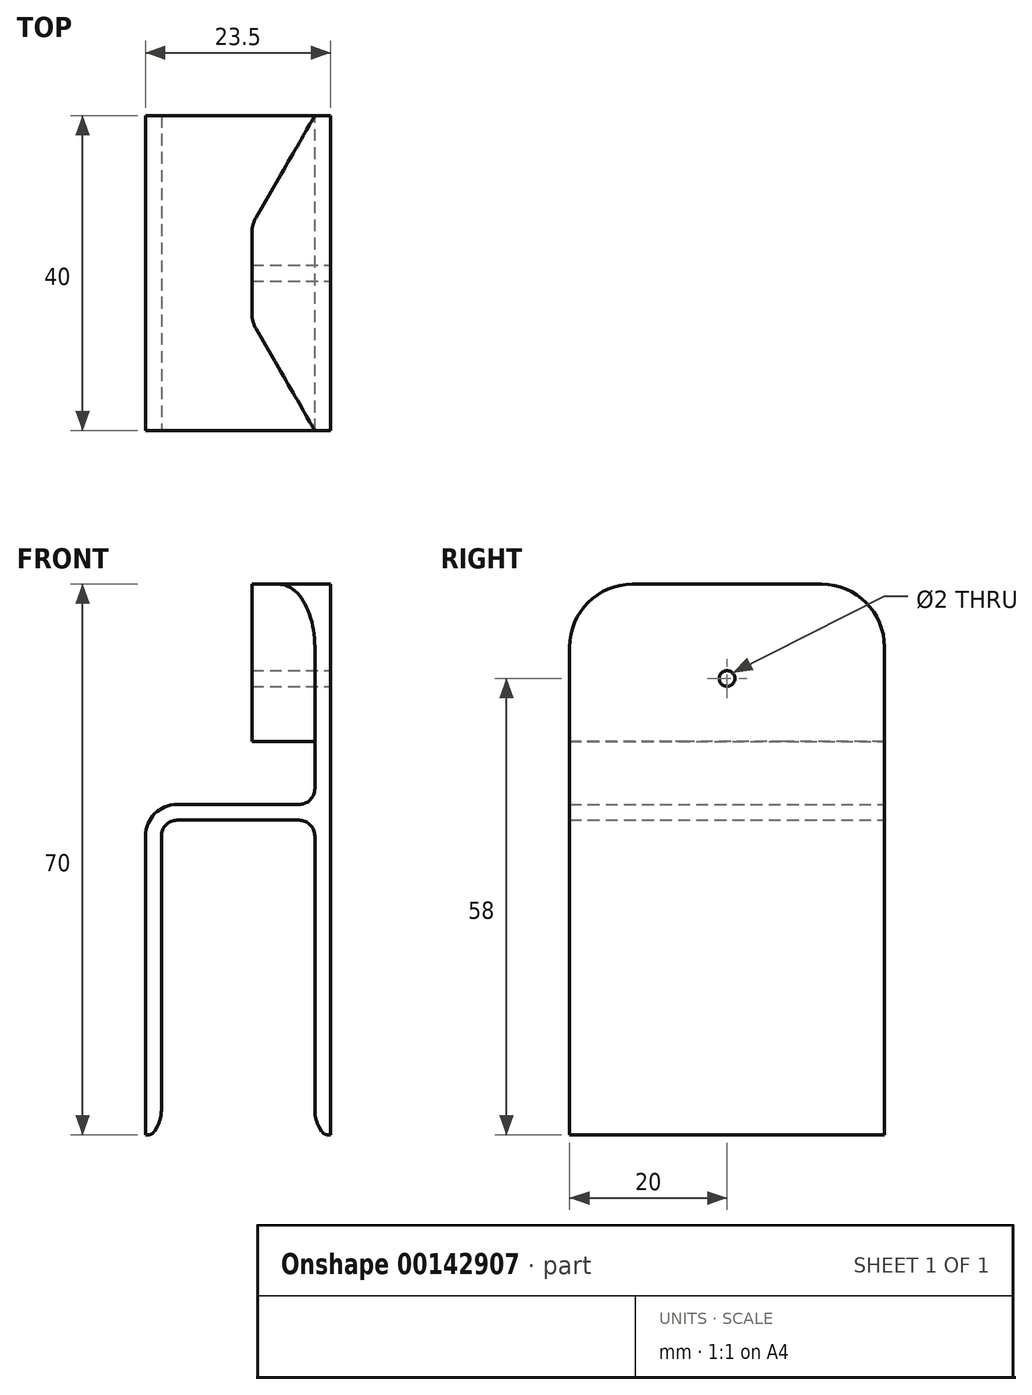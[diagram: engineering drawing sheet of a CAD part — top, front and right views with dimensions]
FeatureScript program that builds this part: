
annotation { "Feature Type Name" : "Feature", "Feature Type Description" : "" }
export const myFeature = defineFeature(function(context is Context, id is Id, definition is map)
    precondition{}
    {
        {
            var Q0;
            Q0=qCreatedBy(makeId("Front.planeOp"),FACE);
            var sketch = newSketch(context, id + "F0", { "sketchPlane" : qUnion([Q0])});
            skLineSegment(sketch, "E0", {"start": v(-19.5, 0) * mm, "end": v(-19.5, -40) * mm});
            skLineSegment(sketch, "E1", {"start": v(-19.5, 0) * mm, "end": v(0, 0) * mm});
            skLineSegment(sketch, "E2", {"start": v(0, 30) * mm, "end": v(0, -40) * mm});
            skLineSegment(sketch, "E3.0", {"start": v(2, 30) * mm, "end": v(2, -40) * mm});
            skLineSegment(sketch, "E4.0", {"start": v(-21.5, 2) * mm, "end": v(0, 2) * mm});
            skLineSegment(sketch, "E5.0", {"start": v(-21.5, 2) * mm, "end": v(-21.5, -40) * mm});
            skLineSegment(sketch, "E6", {"start": v(0, -40) * mm, "end": v(2, -40) * mm});
            skLineSegment(sketch, "E7", {"start": v(-19.5, -40) * mm, "end": v(-21.5, -40) * mm});
            skLineSegment(sketch, "E8", {"start": v(0, 30) * mm, "end": v(2, 30) * mm});
            skSolve(sketch);
        }
        {
            var Q0;
            Q0=makeQuery(id+"F0.imprint","IMPRINT",FACE,{"disambiguationData":[TD([[makeQuery(id+"F0.imprint","IMPRINT",EDGE,{"derivedFrom":sQuery(id+"F0.wireOp",EDGE,"E3.0")}),-1.0]])]});
            var Q1;
            Q1=makeQuery(id+"F0.imprint","IMPRINT",FACE,{"disambiguationData":[TD([[makeQuery(id+"F0.imprint","IMPRINT",EDGE,{"derivedFrom":sQuery(id+"F0.wireOp",EDGE,"E0")}),-1.0]])]});
            extrude(context, id + "F1", {"entities" : qUnion([Q0, Q1]), "depth" : 40 * mm, "symmetric" : true});
        }
        {
            var Q0;
            Q0=makeQuery(id+"F1.opExtrude","SWEPT_FACE",FACE,{"disambiguationData":[OSD([sQuery(id+"F0.wireOp",EDGE,"E8")])]});
            var sketch = newSketch(context, id + "F2", { "sketchPlane" : qUnion([Q0])});
            skLineSegment(sketch, "E9", {"start": v(0, 20) * mm, "end": v(-8, 6.14) * mm});
            skLineSegment(sketch, "E10", {"start": v(-8, 6.14) * mm, "end": v(-8, -6.14) * mm});
            skLineSegment(sketch, "E11", {"start": v(-8, -6.14) * mm, "end": v(0, -20) * mm});
            skSolve(sketch);
        }
        {
            var Q0;
            Q0=makeQuery(id+"F2.imprint","IMPRINT",FACE,{"disambiguationData":[TD([[makeQuery(id+"F2.imprint","IMPRINT",EDGE,{"derivedFrom":sQuery(id+"F2.wireOp",EDGE,"E9")}),1.0]])]});
            extrude(context, id + "F3", {"entities" : qUnion([Q0]), "operationType" : NewBodyOperationType.ADD, "oppositeDirection" : true, "depth" : 20 * mm});
        }
        {
            var Q0;
            Q0=makeQuery(id+"F1.opExtrude","SWEPT_FACE",FACE,{"disambiguationData":[OSD([sQuery(id+"F0.wireOp",EDGE,"E3.0")])]});
            var sketch = newSketch(context, id + "F4", { "sketchPlane" : qUnion([Q0])});
            skLineSegment(sketch, "E12.0", {"start": v(-20, 30) * mm, "end": v(20, 30) * mm});
            skLineSegment(sketch, "E13", {"start": v(0, 30) * mm, "end": v(0, 18) * mm});
            skPoint(sketch, "E13.endSnap0", {"position": v(0, 30) * mm});
            skPoint(sketch, "E14", {"position": v(0, 18) * mm});
            skSolve(sketch);
        }
        {
            var Q0;
            Q0=sQuery(id+"F4.wireOp",VERTEX,"E14");
            var Q1;
            Q1=makeQuery(id+"F1.opExtrude","SWEPT_BODY",BODY,{"disambiguationData":[OSD([sQuery(id+"F0.wireOp",EDGE,"E0"),sQuery(id+"F0.wireOp",EDGE,"E1"),sQuery(id+"F0.wireOp",EDGE,"E2"),sQuery(id+"F0.wireOp",EDGE,"E3.0"),sQuery(id+"F0.wireOp",EDGE,"E4.0"),sQuery(id+"F0.wireOp",EDGE,"E5.0"),sQuery(id+"F0.wireOp",EDGE,"E6"),sQuery(id+"F0.wireOp",EDGE,"E7"),sQuery(id+"F0.wireOp",EDGE,"E8")])]});
            hole(context, id + "F5", {"style" : HoleStyle.SIMPLE, "endStyle" : HoleEndStyle.THROUGH, "holeDiameter" : 2 * mm, "startFromSketch" : true, "locations" : qUnion([Q0]), "scope" : qUnion([Q1]), "isTappedThrough" : true});
        }
        {
            var Q0;
            Q0=makeQuery(id+"F1.opExtrude","SWEPT_EDGE",EDGE,{"disambiguationData":[OSD([sQuery(id+"F0.wireOp",EDGE,"E0"),sQuery(id+"F0.wireOp",EDGE,"E7")])]});
            chamfer(context, id + "F6", {"entities" : qUnion([Q0]), "chamferType" : ChamferType.OFFSET_ANGLE, "width" : 2 * mm, "oppositeDirection" : false, "angle" : 30 * degree});
        }
        {
            var Q0;
            Q0=makeQuery(id+"F1.opExtrude","SWEPT_EDGE",EDGE,{"disambiguationData":[OSD([sQuery(id+"F0.wireOp",EDGE,"E2"),sQuery(id+"F0.wireOp",EDGE,"E6")])]});
            chamfer(context, id + "F7", {"entities" : qUnion([Q0]), "chamferType" : ChamferType.OFFSET_ANGLE, "width" : 2 * mm, "oppositeDirection" : true, "angle" : 30 * degree});
        }
        {
            var Q0;
            {var subQ0=sQuery(id+"F0.wireOp",EDGE,"E7");Q0=makeQuery(id+"F6.opChamfer","BLEND_EDGE",EDGE,{"blendedFrom":[makeQuery(id+"F1.opExtrude","SWEPT_EDGE",EDGE,{"disambiguationData":[OSD([sQuery(id+"F0.wireOp",EDGE,"E0"),subQ0])]}),makeQuery(id+"F1.opExtrude","SWEPT_FACE",FACE,{"disambiguationData":[OSD([subQ0])]})],"blendedInto":[makeQuery(id+"F1.opExtrude","SWEPT_FACE",FACE,{"disambiguationData":[OSD([subQ0])]})]});}
            var Q1;
            {var subQ0=sQuery(id+"F0.wireOp",EDGE,"E6");Q1=makeQuery(id+"F7.opChamfer","BLEND_EDGE",EDGE,{"blendedFrom":[makeQuery(id+"F1.opExtrude","SWEPT_EDGE",EDGE,{"disambiguationData":[OSD([sQuery(id+"F0.wireOp",EDGE,"E2"),subQ0])]}),makeQuery(id+"F1.opExtrude","SWEPT_FACE",FACE,{"disambiguationData":[OSD([subQ0])]})],"blendedInto":[makeQuery(id+"F1.opExtrude","SWEPT_FACE",FACE,{"disambiguationData":[OSD([subQ0])]})]});}
            fillet(context, id + "F8", {"entities" : qUnion([Q0, Q1]), "radius" : 1 * mm, "tangentPropagation" : true, "allowEdgeOverflow" : false});
        }
        {
            var Q0;
            Q0=makeQuery(id+"F1.opExtrude","SWEPT_EDGE",EDGE,{"disambiguationData":[OSD([sQuery(id+"F0.wireOp",EDGE,"E2"),sQuery(id+"F0.wireOp",EDGE,"E4.0")])]});
            var Q1;
            Q1=makeQuery(id+"F1.opExtrude","SWEPT_EDGE",EDGE,{"disambiguationData":[OSD([sQuery(id+"F0.wireOp",EDGE,"E0"),sQuery(id+"F0.wireOp",EDGE,"E1")])]});
            var Q2;
            Q2=makeQuery(id+"F1.opExtrude","SWEPT_EDGE",EDGE,{"disambiguationData":[OSD([sQuery(id+"F0.wireOp",EDGE,"E1"),sQuery(id+"F0.wireOp",EDGE,"E2")])]});
            var Q3;
            Q3=makeQuery(id+"F3.opExtrude","CAP_EDGE",EDGE,{"disambiguationData":[OSD([sQuery(id+"F0.wireOp",EDGE,"E2"),sQuery(id+"F0.wireOp",EDGE,"E8")])],"isStart":false});
            fillet(context, id + "F9", {"entities" : qUnion([Q0, Q1, Q2, Q3]), "radius" : 2 * mm, "tangentPropagation" : true, "allowEdgeOverflow" : false});
        }
        {
            var Q0;
            Q0=makeQuery(id+"F1.opExtrude","SWEPT_EDGE",EDGE,{"disambiguationData":[OSD([sQuery(id+"F0.wireOp",EDGE,"E4.0"),sQuery(id+"F0.wireOp",EDGE,"E5.0")])]});
            var Q1;
            Q1=makeQuery(id+"F3.opExtrude","SWEPT_EDGE",EDGE,{"disambiguationData":[OSD([sQuery(id+"F2.wireOp",EDGE,"E10"),sQuery(id+"F2.wireOp",EDGE,"E11")])]});
            var Q2;
            Q2=makeQuery(id+"F3.opExtrude","SWEPT_EDGE",EDGE,{"disambiguationData":[OSD([sQuery(id+"F2.wireOp",EDGE,"E9"),sQuery(id+"F2.wireOp",EDGE,"E10")])]});
            var Q3;
            {var subQ0=sQuery(id+"F0.wireOp",EDGE,"E0");Q3=makeQuery(id+"F6.opChamfer","BLEND_EDGE",EDGE,{"blendedFrom":[makeQuery(id+"F1.opExtrude","SWEPT_EDGE",EDGE,{"disambiguationData":[OSD([subQ0,sQuery(id+"F0.wireOp",EDGE,"E7")])]}),makeQuery(id+"F1.opExtrude","SWEPT_FACE",FACE,{"disambiguationData":[OSD([subQ0])]})],"blendedInto":[makeQuery(id+"F1.opExtrude","SWEPT_FACE",FACE,{"disambiguationData":[OSD([subQ0])]})]});}
            var Q4;
            {var subQ0=sQuery(id+"F0.wireOp",EDGE,"E2");var subQ1=sQuery(id+"F0.wireOp",EDGE,"E6");Q4=makeQuery(id+"F7.opChamfer","BLEND_EDGE",EDGE,{"blendedFrom":[makeQuery(id+"F1.opExtrude","SWEPT_EDGE",EDGE,{"disambiguationData":[OSD([subQ0,subQ1])]}),makeQuery(id+"F1.opExtrude","SWEPT_FACE",FACE,{"disambiguationData":[OSD([subQ0]),TDD([makeQuery(id+"F0.imprint","IMPRINT",EDGE,{"disambiguationData":[TD([[makeQuery(id+"F0.imprint","INTERSECT",VERTEX,{"derivedFrom":[sQuery(id+"F0.wireOp",EDGE,"E1"),subQ0]}),-1.0]])],"derivedFrom":subQ0})])]})],"blendedInto":[makeQuery(id+"F1.opExtrude","SWEPT_FACE",FACE,{"disambiguationData":[OSD([subQ0]),TDD([makeQuery(id+"F0.imprint","IMPRINT",EDGE,{"disambiguationData":[TD([[makeQuery(id+"F0.imprint","INTERSECT",VERTEX,{"derivedFrom":[sQuery(id+"F0.wireOp",EDGE,"E1"),subQ0]}),-1.0]])],"derivedFrom":subQ0})])]})]});}
            fillet(context, id + "F10", {"entities" : qUnion([Q0, Q1, Q2, Q3, Q4]), "radius" : 4 * mm, "tangentPropagation" : true, "allowEdgeOverflow" : false});
        }
        {
            var Q0;
            Q0=makeQuery(id+"F1.opExtrude","CAP_EDGE",EDGE,{"disambiguationData":[OSD([sQuery(id+"F0.wireOp",EDGE,"E8")])],"isStart":false});
            var Q1;
            Q1=makeQuery(id+"F1.opExtrude","CAP_EDGE",EDGE,{"disambiguationData":[OSD([sQuery(id+"F0.wireOp",EDGE,"E8")])],"isStart":true});
            fillet(context, id + "F11", {"entities" : qUnion([Q0, Q1]), "radius" : 8 * mm, "tangentPropagation" : true, "allowEdgeOverflow" : false});
        }
    });
